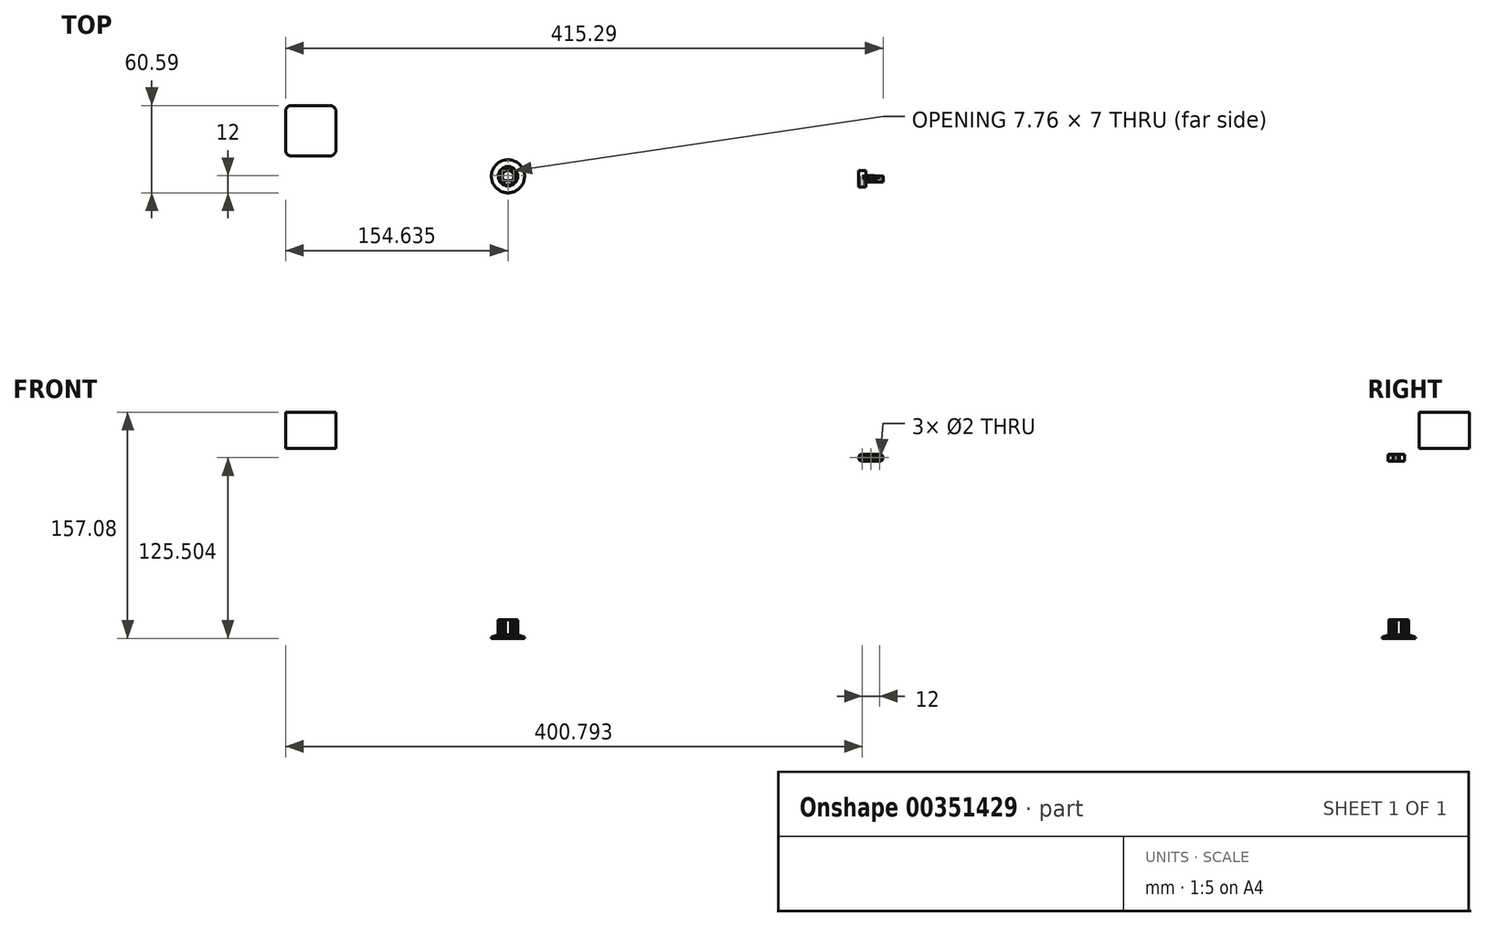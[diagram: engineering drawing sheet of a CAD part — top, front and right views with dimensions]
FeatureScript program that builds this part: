
annotation { "Feature Type Name" : "Feature", "Feature Type Description" : "" }
export const myFeature = defineFeature(function(context is Context, id is Id, definition is map)
    precondition{}
    {
        {
            var Q0;
            Q0=qCreatedBy(makeId("Front.planeOp"),FACE);
            var sketch = newSketch(context, id + "F0", { "sketchPlane" : qUnion([Q0])});
            skCircle(sketch, "E0", {"center": v(206.9, -6.58) * mm, "radius": 1 * mm});
            skCircle(sketch, "E1", {"center": v(212.9, -6.58) * mm, "radius": 1 * mm});
            skCircle(sketch, "E2", {"center": v(218.9, -6.58) * mm, "radius": 1 * mm});
            skCircle(sketch, "E3", {"center": v(206.9, -6.58) * mm, "radius": 2.45 * mm});
            skCircle(sketch, "E4", {"center": v(212.9, -6.58) * mm, "radius": 2.5 * mm});
            skCircle(sketch, "E5", {"center": v(218.9, -6.58) * mm, "radius": 2.5 * mm});
            skLineSegment(sketch, "E6", {"start": v(206.9, -4.13) * mm, "end": v(218.9, -4.08) * mm});
            skLineSegment(sketch, "E7", {"start": v(206.9, -9.03) * mm, "end": v(218.9, -9.08) * mm});
            skLineSegment(sketch, "E8", {"start": v(209.3, -6.08) * mm, "end": v(210.45, -6.08) * mm});
            skLineSegment(sketch, "E9", {"start": v(209.3, -7.08) * mm, "end": v(210.45, -7.08) * mm});
            skPoint(sketch, "E10.orphan", {"position": v(206.9, -6.08) * mm});
            skPoint(sketch, "E11.orphan", {"position": v(206.9, -7.08) * mm});
            skLineSegment(sketch, "E12.trimOffspring", {"start": v(215.35, -7.08) * mm, "end": v(216.45, -7.08) * mm});
            skLineSegment(sketch, "E13.trimOffspring", {"start": v(215.35, -6.08) * mm, "end": v(216.45, -6.08) * mm});
            skSolve(sketch);
        }
        {
            var Q0;
            Q0=makeQuery(id+"F0.imprint","IMPRINT",FACE,{"disambiguationData":[TD([[makeQuery(id+"F0.imprint","IMPRINT",EDGE,{"derivedFrom":sQuery(id+"F0.wireOp",EDGE,"E0")}),-1.0]])]});
            extrude(context, id + "F1", {"entities" : qUnion([Q0]), "depth" : 7.5 * mm, "offsetDistance" : 25 * mm});
        }
        {
            var Q0;
            Q0=makeQuery(id+"F0.imprint","IMPRINT",FACE,{"disambiguationData":[TD([[makeQuery(id+"F0.imprint","IMPRINT",EDGE,{"derivedFrom":sQuery(id+"F0.wireOp",EDGE,"E1")}),-1.0]])]});
            var Q1;
            Q1=makeQuery(id+"F0.imprint","IMPRINT",FACE,{"disambiguationData":[TD([[makeQuery(id+"F0.imprint","IMPRINT",EDGE,{"derivedFrom":sQuery(id+"F0.wireOp",EDGE,"E2")}),-1.0]])]});
            var Q2;
            {var subQ0=sQuery(id+"F0.wireOp",EDGE,"E8");Q2=makeQuery(id+"F0.imprint","IMPRINT",FACE,{"disambiguationData":[TD([[makeQuery(id+"F0.imprint","IMPRINT",EDGE,{"derivedFrom":subQ0}),-1.0]])]});}
            var Q3;
            {var subQ0=sQuery(id+"F0.wireOp",EDGE,"E12.trimOffspring");Q3=makeQuery(id+"F0.imprint","IMPRINT",FACE,{"disambiguationData":[TD([[makeQuery(id+"F0.imprint","IMPRINT",EDGE,{"derivedFrom":subQ0}),1.0]])]});}
            extrude(context, id + "F2", {"entities" : qUnion([Q0, Q1, Q2, Q3]), "operationType" : NewBodyOperationType.ADD, "depth" : 4 * mm, "offsetDistance" : 25 * mm});
        }
        {
            var Q0;
            {var subQ3=sQuery(id+"F0.wireOp",EDGE,"E9");Q0=makeQuery(id+"F0.imprint","IMPRINT",FACE,{"disambiguationData":[TD([[makeQuery(id+"F0.imprint","IMPRINT",EDGE,{"derivedFrom":subQ3}),-1.0]])]});}
            var Q1;
            {var subQ0=sQuery(id+"F0.wireOp",EDGE,"E12.trimOffspring");Q1=makeQuery(id+"F0.imprint","IMPRINT",FACE,{"disambiguationData":[TD([[makeQuery(id+"F0.imprint","IMPRINT",EDGE,{"derivedFrom":subQ0}),-1.0]])]});}
            var Q2;
            {var subQ0=sQuery(id+"F0.wireOp",EDGE,"E13.trimOffspring");Q2=makeQuery(id+"F0.imprint","IMPRINT",FACE,{"disambiguationData":[TD([[makeQuery(id+"F0.imprint","IMPRINT",EDGE,{"derivedFrom":subQ0}),1.0]])]});}
            var Q3;
            {var subQ3=sQuery(id+"F0.wireOp",EDGE,"E8");Q3=makeQuery(id+"F0.imprint","IMPRINT",FACE,{"disambiguationData":[TD([[makeQuery(id+"F0.imprint","IMPRINT",EDGE,{"derivedFrom":subQ3}),1.0]])]});}
            extrude(context, id + "F3", {"entities" : qUnion([Q0, Q1, Q2, Q3]), "operationType" : NewBodyOperationType.ADD, "depth" : 1 * mm, "offsetDistance" : 25 * mm});
        }
        {
            var Q0;
            Q0=makeQuery(id+"F0.imprint","IMPRINT",FACE,{"disambiguationData":[TD([[makeQuery(id+"F0.imprint","IMPRINT",EDGE,{"derivedFrom":sQuery(id+"F0.wireOp",EDGE,"E0")}),-1.0]])]});
            extrude(context, id + "F4", {"entities" : qUnion([Q0]), "operationType" : NewBodyOperationType.ADD, "oppositeDirection" : true, "depth" : 4 * mm, "offsetDistance" : 25 * mm});
        }
        {
            var Q0;
            Q0=makeQuery(id+"F0.imprint","IMPRINT",FACE,{"disambiguationData":[TD([[makeQuery(id+"F0.imprint","IMPRINT",EDGE,{"derivedFrom":sQuery(id+"F0.wireOp",EDGE,"E1")}),-1.0]])]});
            extrude(context, id + "F5", {"entities" : qUnion([Q0]), "operationType" : NewBodyOperationType.ADD, "oppositeDirection" : true, "depth" : 0.5 * mm, "offsetDistance" : 25 * mm});
        }
        {
            var Q0;
            Q0=qCreatedBy(makeId("Front.planeOp"),FACE);
            var sketch = newSketch(context, id + "F6", { "sketchPlane" : qUnion([Q0])});
            skLineSegment(sketch, "E14", {"start": v(-39.25, -88.38) * mm, "end": v(-39.25, -184.57) * mm});
            skLineSegment(sketch, "E15", {"start": v(-27.75, -132.08) * mm, "end": v(-27.75, -131.08) * mm});
            skLineSegment(sketch, "E16", {"start": v(-33.6, -119.28) * mm, "end": v(-33.6, -129.48) * mm});
            skLineSegment(sketch, "E17", {"start": v(-33.6, -129.48) * mm, "end": v(-32.6, -129.48) * mm});
            skLineSegment(sketch, "E18", {"start": v(-32.6, -129.48) * mm, "end": v(-27.75, -131.08) * mm});
            skPoint(sketch, "E19.endSnap0", {"position": v(-39.25, -136.47) * mm});
            skLineSegment(sketch, "E20", {"start": v(-35.25, -132.08) * mm, "end": v(-35.25, -119.28) * mm});
            skLineSegment(sketch, "E21", {"start": v(-27.75, -132.08) * mm, "end": v(-35.25, -132.08) * mm});
            skLineSegment(sketch, "E22", {"start": v(-33.6, -119.28) * mm, "end": v(-35.25, -119.28) * mm});
            skSolve(sketch);
        }
        {
            var Q0;
            Q0=makeQuery(id+"F6.imprint","IMPRINT",FACE,{"disambiguationData":[TD([[makeQuery(id+"F6.imprint","IMPRINT",EDGE,{"derivedFrom":sQuery(id+"F6.wireOp",EDGE,"osBOGFwN-gBvn-ZMXP-haiD-d74Tpin4a2b0")}),1.0]])]});
            var Q1;
            Q1=makeQuery(id+"F6.imprint","IMPRINT",FACE,{"disambiguationData":[TD([[makeQuery(id+"F6.imprint","IMPRINT",EDGE,{"derivedFrom":sQuery(id+"F6.wireOp",EDGE,"E15")}),1.0]])]});
            var Q2;
            Q2=sQuery(id+"F6.wireOp",EDGE,"E14");
            revolve(context, id + "F7", {"entities" : qUnion([Q0, Q1]), "axis" : qUnion([Q2]), "revolveType" : RevolveType.FULL});
        }
        {
            var Q0;
            Q0=makeQuery(id+"F7.opRevolve","SWEPT_FACE",FACE,{"disambiguationData":[OSD([sQuery(id+"F6.wireOp",EDGE,"E22")])]});
            var sketch = newSketch(context, id + "F8", { "sketchPlane" : qUnion([Q0])});
            skCircle(sketch, "E23", {"center": v(-39.25, 0) * mm, "radius": 5.66 * mm});
            skArc(sketch, "E24", {"start": v(-40.52, 6.82) * mm, "mid": v(-40.6, 6.8) * mm, "end": v(-40.7, 6.79) * mm});
            skArc(sketch, "E25", {"start": v(-40.16, 6.54) * mm, "mid": v(-39.25, 5.66) * mm, "end": v(-38.35, 6.54) * mm});
            skPoint(sketch, "E25.first.point", {"position": v(-39.25, 5.66) * mm});
            skPoint(sketch, "E25.second.point", {"position": v(-39.25, 7.48) * mm});
            skPoint(sketch, "E25.third.point", {"position": v(-38.36, 6.71) * mm});
            skPoint(sketch, "E26.visualSharp", {"position": v(-40.1, 6.89) * mm});
            skArc(sketch, "E26.filletArc", {"start": v(-40.16, 6.54) * mm, "mid": v(-40.28, 6.76) * mm, "end": v(-40.52, 6.82) * mm});
            skPoint(sketch, "E27.visualSharp", {"position": v(-38.4, 6.89) * mm});
            skArc(sketch, "E27.filletArc", {"start": v(-38, 6.82) * mm, "mid": v(-38.23, 6.76) * mm, "end": v(-38.35, 6.54) * mm});
            skArc(sketch, "E28.1.0", {"start": v(-42.6, 5.7) * mm, "mid": v(-42.79, 5.86) * mm, "end": v(-43.03, 5.82) * mm});
            skArc(sketch, "E28.1.1", {"start": v(-42.6, 5.7) * mm, "mid": v(-41.42, 5.23) * mm, "end": v(-40.92, 6.39) * mm});
            skArc(sketch, "E28.1.2", {"start": v(-40.7, 6.79) * mm, "mid": v(-40.9, 6.64) * mm, "end": v(-40.92, 6.39) * mm});
            skArc(sketch, "E28.2.0", {"start": v(-44.52, 3.98) * mm, "mid": v(-44.76, 4.06) * mm, "end": v(-44.97, 3.93) * mm});
            skArc(sketch, "E28.2.1", {"start": v(-44.52, 3.98) * mm, "mid": v(-43.26, 4) * mm, "end": v(-43.24, 5.27) * mm});
            skArc(sketch, "E28.2.2", {"start": v(-43.19, 5.72) * mm, "mid": v(-43.31, 5.5) * mm, "end": v(-43.24, 5.27) * mm});
            skArc(sketch, "E28.3.0", {"start": v(-45.64, 1.66) * mm, "mid": v(-45.9, 1.64) * mm, "end": v(-46.04, 1.44) * mm});
            skArc(sketch, "E28.3.1", {"start": v(-45.64, 1.66) * mm, "mid": v(-44.48, 2.17) * mm, "end": v(-44.95, 3.34) * mm});
            skArc(sketch, "E28.3.2", {"start": v(-45.08, 3.78) * mm, "mid": v(-45.11, 3.53) * mm, "end": v(-44.95, 3.34) * mm});
            skArc(sketch, "E28.4.0", {"start": v(-45.8, -0.9) * mm, "mid": v(-46.02, -1.02) * mm, "end": v(-46.08, -1.26) * mm});
            skArc(sketch, "E28.4.1", {"start": v(-45.8, -0.9) * mm, "mid": v(-44.91, 0) * mm, "end": v(-45.8, 0.9) * mm});
            skArc(sketch, "E28.4.2", {"start": v(-46.08, 1.26) * mm, "mid": v(-46.02, 1.02) * mm, "end": v(-45.8, 0.9) * mm});
            skArc(sketch, "E28.5.0", {"start": v(-44.95, -3.34) * mm, "mid": v(-45.11, -3.53) * mm, "end": v(-45.08, -3.78) * mm});
            skArc(sketch, "E28.5.1", {"start": v(-44.95, -3.34) * mm, "mid": v(-44.48, -2.17) * mm, "end": v(-45.64, -1.66) * mm});
            skArc(sketch, "E28.5.2", {"start": v(-46.04, -1.44) * mm, "mid": v(-45.9, -1.64) * mm, "end": v(-45.64, -1.66) * mm});
            skArc(sketch, "E28.6.0", {"start": v(-43.24, -5.27) * mm, "mid": v(-43.31, -5.5) * mm, "end": v(-43.19, -5.72) * mm});
            skArc(sketch, "E28.6.1", {"start": v(-43.24, -5.27) * mm, "mid": v(-43.26, -4) * mm, "end": v(-44.52, -3.98) * mm});
            skArc(sketch, "E28.6.2", {"start": v(-44.97, -3.93) * mm, "mid": v(-44.76, -4.06) * mm, "end": v(-44.52, -3.98) * mm});
            skArc(sketch, "E28.7.0", {"start": v(-40.92, -6.39) * mm, "mid": v(-40.9, -6.64) * mm, "end": v(-40.7, -6.79) * mm});
            skArc(sketch, "E28.7.1", {"start": v(-40.92, -6.39) * mm, "mid": v(-41.42, -5.23) * mm, "end": v(-42.6, -5.7) * mm});
            skArc(sketch, "E28.7.2", {"start": v(-43.03, -5.82) * mm, "mid": v(-42.79, -5.86) * mm, "end": v(-42.6, -5.7) * mm});
            skArc(sketch, "E28.8.0", {"start": v(-38.34, -6.54) * mm, "mid": v(-38.23, -6.76) * mm, "end": v(-38, -6.82) * mm});
            skArc(sketch, "E28.8.1", {"start": v(-38.34, -6.54) * mm, "mid": v(-39.25, -5.66) * mm, "end": v(-40.16, -6.54) * mm});
            skArc(sketch, "E28.8.2", {"start": v(-40.52, -6.82) * mm, "mid": v(-40.28, -6.76) * mm, "end": v(-40.16, -6.54) * mm});
            skArc(sketch, "E28.9.0", {"start": v(-35.91, -5.7) * mm, "mid": v(-35.72, -5.86) * mm, "end": v(-35.48, -5.82) * mm});
            skArc(sketch, "E28.9.1", {"start": v(-35.91, -5.7) * mm, "mid": v(-37.09, -5.23) * mm, "end": v(-37.6, -6.39) * mm});
            skArc(sketch, "E28.9.2", {"start": v(-37.81, -6.79) * mm, "mid": v(-37.61, -6.64) * mm, "end": v(-37.6, -6.39) * mm});
            skArc(sketch, "E28.10.0", {"start": v(-33.99, -3.98) * mm, "mid": v(-33.75, -4.06) * mm, "end": v(-33.54, -3.93) * mm});
            skArc(sketch, "E28.10.1", {"start": v(-33.99, -3.98) * mm, "mid": v(-35.25, -4) * mm, "end": v(-35.27, -5.27) * mm});
            skArc(sketch, "E28.10.2", {"start": v(-35.32, -5.72) * mm, "mid": v(-35.2, -5.5) * mm, "end": v(-35.27, -5.27) * mm});
            skArc(sketch, "E28.11.0", {"start": v(-32.87, -1.66) * mm, "mid": v(-32.62, -1.64) * mm, "end": v(-32.47, -1.44) * mm});
            skArc(sketch, "E28.11.1", {"start": v(-32.87, -1.66) * mm, "mid": v(-34.03, -2.17) * mm, "end": v(-33.56, -3.34) * mm});
            skArc(sketch, "E28.11.2", {"start": v(-33.43, -3.78) * mm, "mid": v(-33.4, -3.53) * mm, "end": v(-33.56, -3.34) * mm});
            skArc(sketch, "E28.12.0", {"start": v(-32.72, 0.9) * mm, "mid": v(-32.5, 1.02) * mm, "end": v(-32.43, 1.26) * mm});
            skArc(sketch, "E28.12.1", {"start": v(-32.72, 0.9) * mm, "mid": v(-33.6, 0) * mm, "end": v(-32.72, -0.9) * mm});
            skArc(sketch, "E28.12.2", {"start": v(-32.43, -1.26) * mm, "mid": v(-32.5, -1.02) * mm, "end": v(-32.72, -0.9) * mm});
            skArc(sketch, "E28.13.0", {"start": v(-33.56, 3.34) * mm, "mid": v(-33.4, 3.53) * mm, "end": v(-33.43, 3.78) * mm});
            skArc(sketch, "E28.13.1", {"start": v(-33.56, 3.34) * mm, "mid": v(-34.03, 2.17) * mm, "end": v(-32.87, 1.66) * mm});
            skArc(sketch, "E28.13.2", {"start": v(-32.47, 1.44) * mm, "mid": v(-32.62, 1.64) * mm, "end": v(-32.87, 1.66) * mm});
            skArc(sketch, "E28.14.0", {"start": v(-35.27, 5.27) * mm, "mid": v(-35.2, 5.5) * mm, "end": v(-35.32, 5.72) * mm});
            skArc(sketch, "E28.14.1", {"start": v(-35.27, 5.27) * mm, "mid": v(-35.25, 4) * mm, "end": v(-33.99, 3.98) * mm});
            skArc(sketch, "E28.14.2", {"start": v(-33.54, 3.93) * mm, "mid": v(-33.75, 4.06) * mm, "end": v(-33.99, 3.98) * mm});
            skArc(sketch, "E28.15.0", {"start": v(-37.6, 6.39) * mm, "mid": v(-37.61, 6.64) * mm, "end": v(-37.81, 6.79) * mm});
            skArc(sketch, "E28.15.1", {"start": v(-37.6, 6.39) * mm, "mid": v(-37.09, 5.23) * mm, "end": v(-35.91, 5.7) * mm});
            skArc(sketch, "E28.15.2", {"start": v(-35.48, 5.82) * mm, "mid": v(-35.72, 5.86) * mm, "end": v(-35.91, 5.7) * mm});
            skArc(sketch, "E29.trimOffspring", {"start": v(-43.03, 5.82) * mm, "mid": v(-43.11, 5.77) * mm, "end": v(-43.19, 5.72) * mm});
            skArc(sketch, "E30.trimOffspring", {"start": v(-37.81, 6.79) * mm, "mid": v(-37.9, 6.8) * mm, "end": v(-38, 6.82) * mm});
            skArc(sketch, "E31.trimOffspring", {"start": v(-44.97, 3.93) * mm, "mid": v(-45.03, 3.86) * mm, "end": v(-45.08, 3.78) * mm});
            skArc(sketch, "E32.trimOffspring", {"start": v(-46.04, 1.44) * mm, "mid": v(-46.06, 1.35) * mm, "end": v(-46.08, 1.26) * mm});
            skArc(sketch, "E33.trimOffspring", {"start": v(-46.08, -1.26) * mm, "mid": v(-46.06, -1.35) * mm, "end": v(-46.04, -1.44) * mm});
            skArc(sketch, "E34.trimOffspring", {"start": v(-45.08, -3.78) * mm, "mid": v(-45.02, -3.86) * mm, "end": v(-44.97, -3.93) * mm});
            skArc(sketch, "E35.trimOffspring", {"start": v(-43.19, -5.72) * mm, "mid": v(-43.11, -5.77) * mm, "end": v(-43.03, -5.82) * mm});
            skArc(sketch, "E36.trimOffspring", {"start": v(-40.7, -6.79) * mm, "mid": v(-40.6, -6.8) * mm, "end": v(-40.52, -6.82) * mm});
            skArc(sketch, "E37.trimOffspring", {"start": v(-38, -6.82) * mm, "mid": v(-37.9, -6.8) * mm, "end": v(-37.81, -6.79) * mm});
            skArc(sketch, "E38.trimOffspring", {"start": v(-35.48, -5.82) * mm, "mid": v(-35.4, -5.77) * mm, "end": v(-35.32, -5.72) * mm});
            skArc(sketch, "E39.trimOffspring", {"start": v(-33.54, -3.93) * mm, "mid": v(-33.48, -3.86) * mm, "end": v(-33.43, -3.78) * mm});
            skArc(sketch, "E40.trimOffspring", {"start": v(-32.47, -1.44) * mm, "mid": v(-32.45, -1.35) * mm, "end": v(-32.43, -1.26) * mm});
            skArc(sketch, "E41.trimOffspring", {"start": v(-32.43, 1.26) * mm, "mid": v(-32.45, 1.35) * mm, "end": v(-32.47, 1.44) * mm});
            skArc(sketch, "E42.trimOffspring", {"start": v(-33.43, 3.78) * mm, "mid": v(-33.48, 3.86) * mm, "end": v(-33.54, 3.93) * mm});
            skArc(sketch, "E43.trimOffspring", {"start": v(-35.32, 5.72) * mm, "mid": v(-35.4, 5.77) * mm, "end": v(-35.48, 5.82) * mm});
            skLineSegment(sketch, "E44", {"start": v(-41.9, -3) * mm, "end": v(-36.6, -3) * mm});
            skArc(sketch, "E45", {"start": v(-36.6, -3) * mm, "mid": v(-39.25, 4) * mm, "end": v(-41.9, -3) * mm});
            skSolve(sketch);
        }
        {
            var Q0;
            Q0 = qSketchRegion(id + "F8", true);
            extrude(context, id + "F9", {"entities" : qUnion([Q0]), "operationType" : NewBodyOperationType.ADD, "oppositeDirection" : true, "depth" : 12.8 * mm, "offsetDistance" : 25 * mm});
        }
        {
            var Q0;
            Q0=qCreatedBy(makeId("Top.planeOp"),FACE);
            var sketch = newSketch(context, id + "F10", { "sketchPlane" : qUnion([Q0])});
            skLineSegment(sketch, "E46.bottom", {"start": v(-189.9, 49.1) * mm, "end": v(-162.9, 49.1) * mm});
            skLineSegment(sketch, "E46.top", {"start": v(-189.9, 14.1) * mm, "end": v(-162.9, 14.1) * mm});
            skLineSegment(sketch, "E46.left", {"start": v(-193.9, 45.1) * mm, "end": v(-193.9, 18.1) * mm});
            skLineSegment(sketch, "E46.right", {"start": v(-158.9, 45.1) * mm, "end": v(-158.9, 18.1) * mm});
            skPoint(sketch, "E47.visualSharp", {"position": v(-193.9, 49.1) * mm});
            skArc(sketch, "E47.filletArc", {"start": v(-189.9, 49.1) * mm, "mid": v(-192.72, 47.92) * mm, "end": v(-193.9, 45.1) * mm});
            skPoint(sketch, "E48.visualSharp", {"position": v(-158.9, 49.1) * mm});
            skArc(sketch, "E48.filletArc", {"start": v(-158.9, 45.1) * mm, "mid": v(-160.06, 47.92) * mm, "end": v(-162.9, 49.1) * mm});
            skPoint(sketch, "E49.visualSharp", {"position": v(-158.9, 14.1) * mm});
            skArc(sketch, "E49.filletArc", {"start": v(-162.9, 14.1) * mm, "mid": v(-160.06, 15.26) * mm, "end": v(-158.9, 18.1) * mm});
            skPoint(sketch, "E50.visualSharp", {"position": v(-193.9, 14.1) * mm});
            skArc(sketch, "E50.filletArc", {"start": v(-193.9, 18.1) * mm, "mid": v(-192.72, 15.26) * mm, "end": v(-189.9, 14.1) * mm});
            skSolve(sketch);
        }
        {
            var Q0;
            Q0 = qSketchRegion(id + "F10", true);
            var Q1;
            Q1=makeQuery(id+"F10.imprint","IMPRINT",FACE,{"disambiguationData":[TD([[makeQuery(id+"F10.imprint","IMPRINT",EDGE,{"derivedFrom":sQuery(id+"F10.wireOp",EDGE,"E46.bottom")}),-1.0]])]});
            extrude(context, id + "F11", {"entities" : qUnion([Q0, Q1]), "depth" : 25 * mm, "offsetDistance" : 25 * mm});
        }
    });
